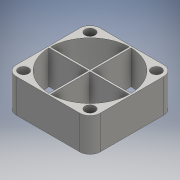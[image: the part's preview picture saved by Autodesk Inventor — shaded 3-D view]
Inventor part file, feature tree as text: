
AUTODESK INVENTOR PART (.ipt)
format: ipt  version: 2016 (Build 200138000, 138)  size: 145,920 bytes
history: native  units: mm
features: sketch x4, extrude x3, hole x1, fillet x1
ambient origin geometry x8: Origin, YZ Plane, XZ Plane, XY Plane, X Axis, Y Axis, Z Axis, Center Point
bodies: Solid1 (feature_tree)
feature tree (9):
  extrude  "Extrusion1"  Depth=25.0mm
  hole  "Hole1"  [1 undecoded]
  fillet  "Fillet1"  [1 undecoded]
  extrude  "Extrusion2"  Depth=3.0mm
  extrude  "Extrusion3"  Depth=10.0mm
  sketch  "Sketch1"  dims[d0=25.0mm d1=25.0mm]
  sketch  "Sketch2"  dims[d2=10.0mm d3=0.0mm d4=28.0mm d5=45.0deg]
  sketch  "Sketch3"  dims[d6=40.0mm d8=360.0deg]
  sketch  "Sketch4"  dims[d10=3.0mm d11=6.0mm d12=4.0mm d13=2.0mm d14=90.0deg d15=15.25mm d16=20.594885mm d17=3.0mm d18=24.0mm d19=10.0mm d20=0.0mm d21=0.5mm d22=0.5mm d23=10.0mm d24=0.0mm]
note: 2 required parameter values undecoded (feature->parameter linkage not recoverable at this tier; creation-order binding heuristic only, values carry confidence <= 0.55)
